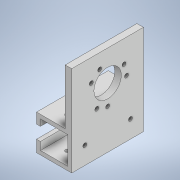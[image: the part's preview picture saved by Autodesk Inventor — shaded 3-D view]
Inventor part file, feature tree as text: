
AUTODESK INVENTOR PART (.ipt)
format: ipt  version: 2022 (Build 260153000, 153)  size: 184,832 bytes
history: native  units: in
note: dims shown in document units (in); Inventor stores cm internally (conversion verified against a paired STEP export)
features: extrude x8, sketch x8, reference x7, other x3
ambient origin geometry x8: Origin, YZ Plane, XZ Plane, XY Plane, X Axis, Y Axis, Z Axis, Center Point
bodies: Solid1 (feature_tree)
feature tree (26):
  extrude  "Extrusion1"  Depth=0.3937in
  extrude  "Extrusion2"  Depth=0.315in TaperAngle=0.0deg
  extrude  "Extrusion3"  Depth=1.6654in TaperAngle=0.0deg
  extrude  "Extrusion4"  Depth=0.748in
  extrude  "Extrusion5"  Depth=1.6654in TaperAngle=0.0deg
  extrude  "Extrusion6"  Depth=1.6654in TaperAngle=0.0deg
  extrude  "Extrusion7"  Depth=0.1181in
  extrude  "Extrusion8"  Depth=0.3937in
  sketch  "Sketch1"  dims[d5=2.1654in d6=0.0in d7=0.3937in]
  reference  "Reference1"
  sketch  "Sketch2"  dims[d8=0.315in d9=0.6029in d10=0.0in]
  sketch  "Sketch3"  dims[d11=0.1969in d12=1.6654in d13=0.0in]
  sketch  "Sketch4"  dims[d14=1.4173in d15=0.748in]
  sketch  "Sketch5"  dims[d16=0.2362in d17=1.6654in d18=0.0in]
  sketch  "Sketch6"  dims[d19=0.8268in d20=1.6654in d21=0.0in]
  reference  "Reference2"
  reference  "Reference3"
  reference  "Reference4"
  reference  "Reference5"
  reference  "Reference6"
  reference  "Reference7"
  sketch  "Sketch7"  dims[d22=1.6654in d23=0.0in d24=0.1181in]
  sketch  "Sketch8"  dims[d25=0.1181in d26=0.3937in d27=0.3937in d28=0.3937in d29=0.0in d30=0.1181in d31=0.1181in d32=0.3937in d33=0.3937in d34=0.0in d35=0.0in d36=0.8268in d37=0.8268in d38=0.1181in d39=0.1181in d40=0.1181in d41=0.1181in]
  parser-record x1  (decoder bookkeeping rows leaked as tree rows — omitted from the tree; the rows remain in map.json)
  other  "model.iam"
  other  "arm:1"
note: 1 file-system path scrubbed to <path> (originals preserved in map.json)
